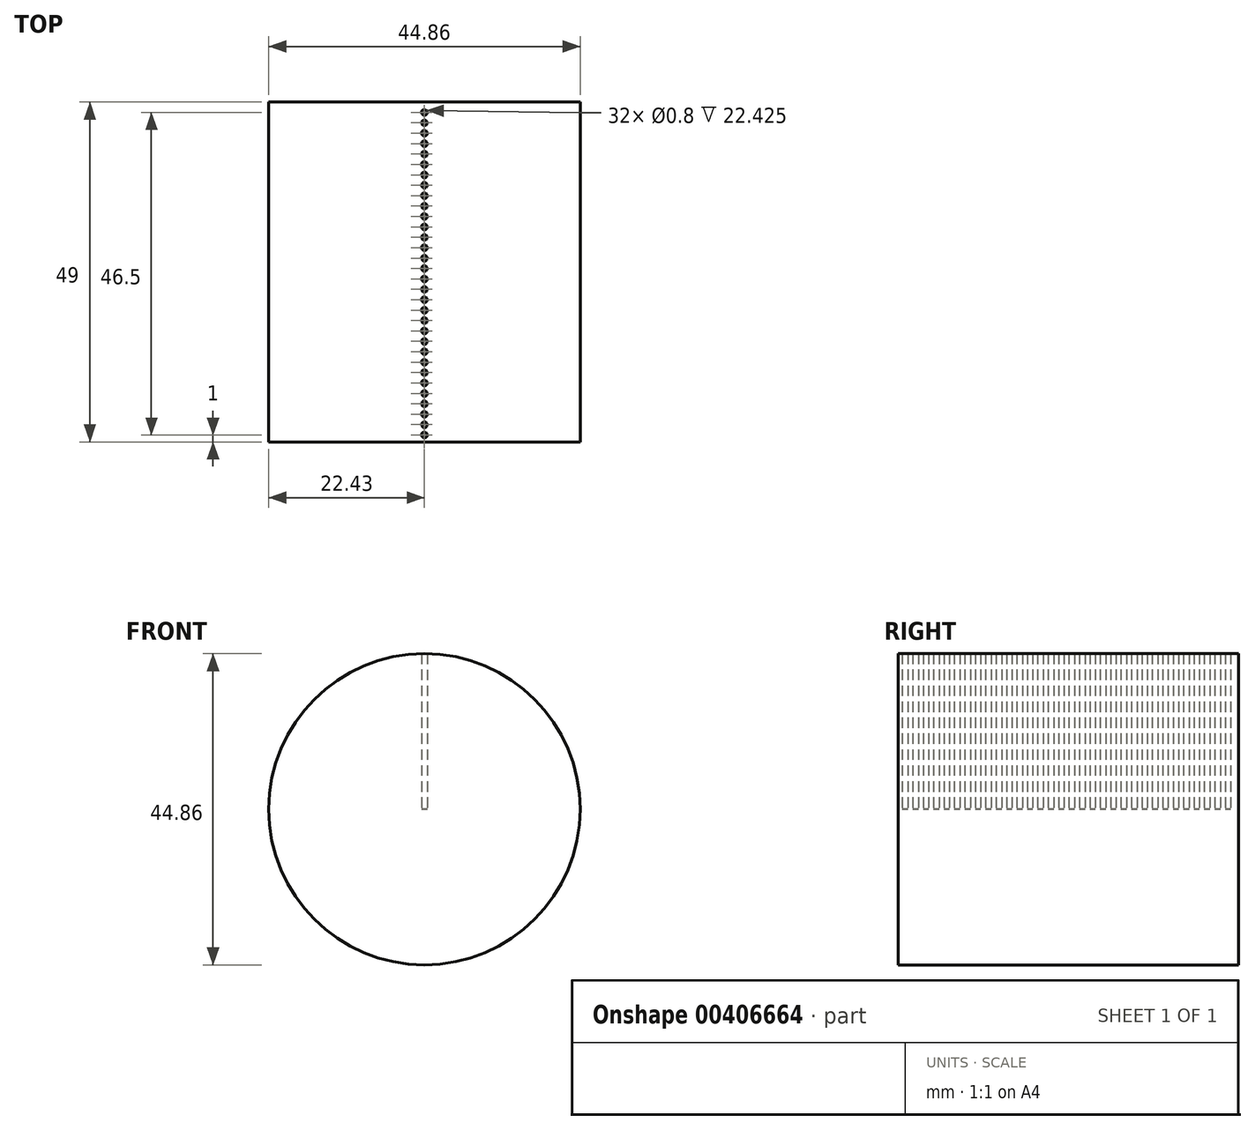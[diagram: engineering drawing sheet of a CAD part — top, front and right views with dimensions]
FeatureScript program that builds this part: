
annotation { "Feature Type Name" : "Feature", "Feature Type Description" : "" }
export const myFeature = defineFeature(function(context is Context, id is Id, definition is map)
    precondition{}
    {
        {
            var Q0;
            Q0=qCreatedBy(makeId("Front.planeOp"),FACE);
            var sketch = newSketch(context, id + "F0", { "sketchPlane" : qUnion([Q0])});
            skCircle(sketch, "E0", {"center": v(0, 0) * mm, "radius": 22.43 * mm});
            skSolve(sketch);
        }
        {
            var Q0;
            Q0 = qSketchRegion(id + "F0", true);
            extrude(context, id + "F1", {"entities" : qUnion([Q0]), "depth" : 49 * mm});
        }
        {
            var Q0;
            Q0=qCreatedBy(makeId("Top.planeOp"),FACE);
            var sketch = newSketch(context, id + "F2", { "sketchPlane" : qUnion([Q0])});
            skCircle(sketch, "E1", {"center": v(0, -1.5) * mm, "radius": 0.4 * mm});
            skCircle(sketch, "E2.1.0.0", {"center": v(0, -3) * mm, "radius": 0.4 * mm});
            skCircle(sketch, "E2.2.0.0", {"center": v(0, -4.5) * mm, "radius": 0.4 * mm});
            skCircle(sketch, "E2.3.0.0", {"center": v(0, -6) * mm, "radius": 0.4 * mm});
            skCircle(sketch, "E2.4.0.0", {"center": v(0, -7.5) * mm, "radius": 0.4 * mm});
            skCircle(sketch, "E2.5.0.0", {"center": v(0, -9) * mm, "radius": 0.4 * mm});
            skCircle(sketch, "E2.6.0.0", {"center": v(0, -10.5) * mm, "radius": 0.4 * mm});
            skCircle(sketch, "E2.7.0.0", {"center": v(0, -12) * mm, "radius": 0.4 * mm});
            skCircle(sketch, "E2.8.0.0", {"center": v(0, -13.5) * mm, "radius": 0.4 * mm});
            skCircle(sketch, "E2.9.0.0", {"center": v(0, -15) * mm, "radius": 0.4 * mm});
            skCircle(sketch, "E2.10.0.0", {"center": v(0, -16.5) * mm, "radius": 0.4 * mm});
            skCircle(sketch, "E2.11.0.0", {"center": v(0, -18) * mm, "radius": 0.4 * mm});
            skCircle(sketch, "E2.12.0.0", {"center": v(0, -19.5) * mm, "radius": 0.4 * mm});
            skCircle(sketch, "E2.13.0.0", {"center": v(0, -21) * mm, "radius": 0.4 * mm});
            skCircle(sketch, "E2.14.0.0", {"center": v(0, -22.5) * mm, "radius": 0.4 * mm});
            skCircle(sketch, "E2.15.0.0", {"center": v(0, -24) * mm, "radius": 0.4 * mm});
            skCircle(sketch, "E2.16.0.0", {"center": v(0, -25.5) * mm, "radius": 0.4 * mm});
            skCircle(sketch, "E2.17.0.0", {"center": v(0, -27) * mm, "radius": 0.4 * mm});
            skCircle(sketch, "E2.18.0.0", {"center": v(0, -28.5) * mm, "radius": 0.4 * mm});
            skCircle(sketch, "E2.19.0.0", {"center": v(0, -30) * mm, "radius": 0.4 * mm});
            skCircle(sketch, "E2.20.0.0", {"center": v(0, -31.5) * mm, "radius": 0.4 * mm});
            skCircle(sketch, "E2.21.0.0", {"center": v(0, -33) * mm, "radius": 0.4 * mm});
            skCircle(sketch, "E2.22.0.0", {"center": v(0, -34.5) * mm, "radius": 0.4 * mm});
            skCircle(sketch, "E2.23.0.0", {"center": v(0, -36) * mm, "radius": 0.4 * mm});
            skCircle(sketch, "E2.24.0.0", {"center": v(0, -37.5) * mm, "radius": 0.4 * mm});
            skCircle(sketch, "E2.25.0.0", {"center": v(0, -39) * mm, "radius": 0.4 * mm});
            skCircle(sketch, "E2.26.0.0", {"center": v(0, -40.5) * mm, "radius": 0.4 * mm});
            skCircle(sketch, "E2.27.0.0", {"center": v(0, -42) * mm, "radius": 0.4 * mm});
            skCircle(sketch, "E2.28.0.0", {"center": v(0, -43.5) * mm, "radius": 0.4 * mm});
            skCircle(sketch, "E2.29.0.0", {"center": v(0, -45) * mm, "radius": 0.4 * mm});
            skCircle(sketch, "E2.30.0.0", {"center": v(0, -46.5) * mm, "radius": 0.4 * mm});
            skCircle(sketch, "E2.31.0.0", {"center": v(0, -48) * mm, "radius": 0.4 * mm});
            skLineSegment(sketch, "E2.direction1", {"start": v(0, -1.5) * mm, "end": v(0, -3) * mm, "construction": true});
            skSolve(sketch);
        }
        {
            var Q0;
            Q0 = qSketchRegion(id + "F2", true);
            extrude(context, id + "F3", {"entities" : qUnion([Q0]), "operationType" : NewBodyOperationType.REMOVE, "depth" : 31 * mm});
        }
    });
